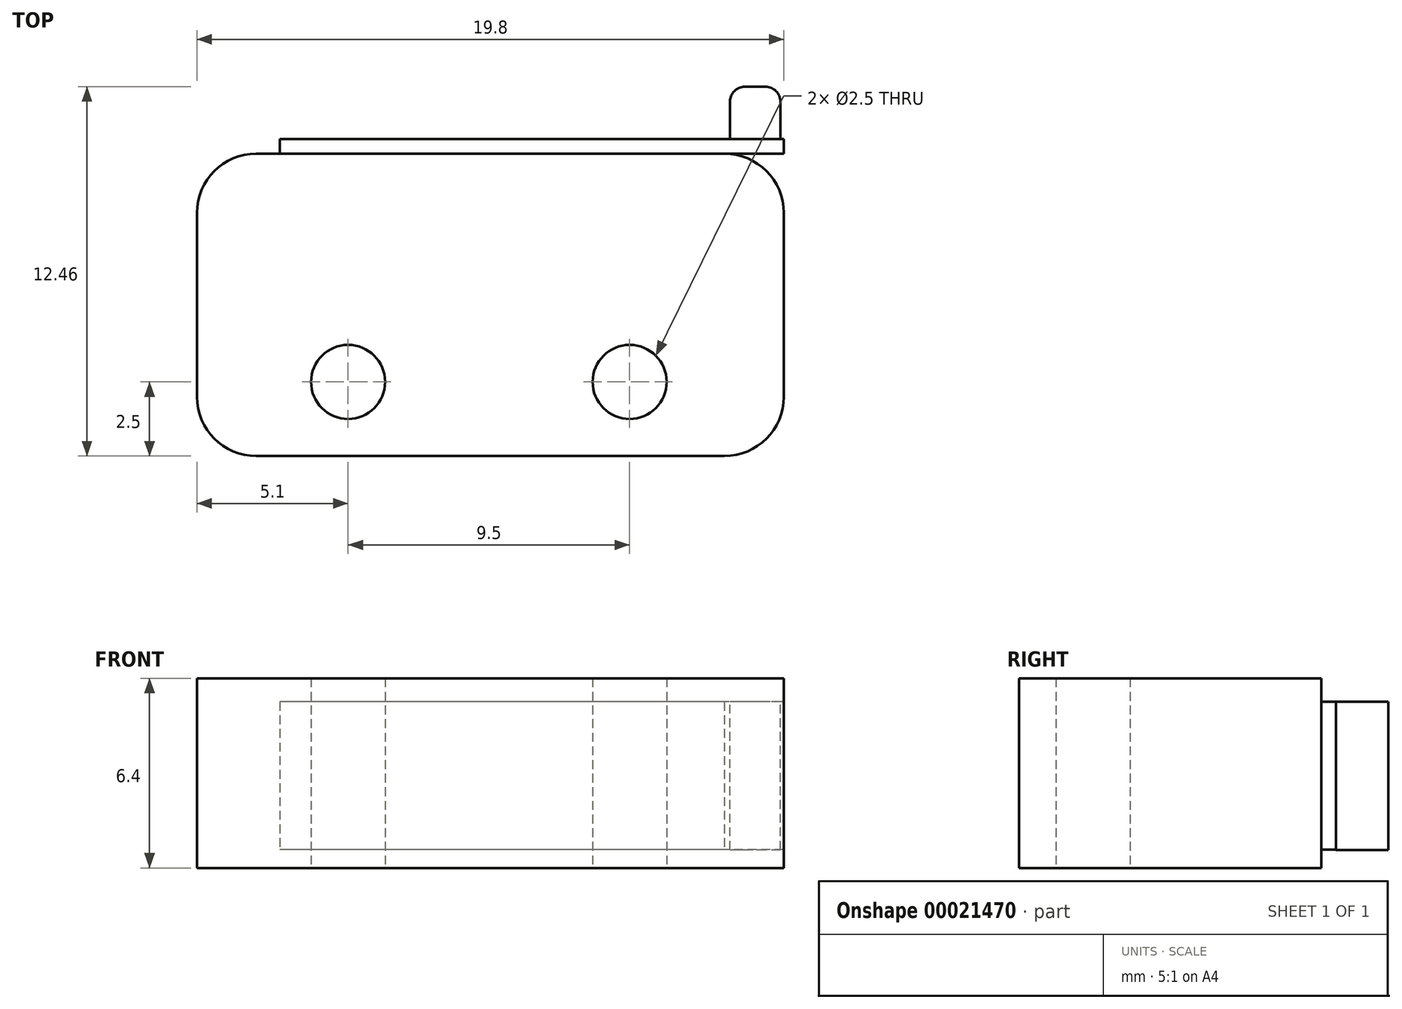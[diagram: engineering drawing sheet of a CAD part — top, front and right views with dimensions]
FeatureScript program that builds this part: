
annotation { "Feature Type Name" : "Feature", "Feature Type Description" : "" }
export const myFeature = defineFeature(function(context is Context, id is Id, definition is map)
    precondition{}
    {
        {
            var Q0;
            Q0=qCreatedBy(makeId("Top.planeOp"),FACE);
            var sketch = newSketch(context, id + "F0", { "sketchPlane" : qUnion([Q0])});
            skLineSegment(sketch, "E0.rect.bottom", {"start": v(9.9, -5.1) * mm, "end": v(-9.9, -5.1) * mm});
            skLineSegment(sketch, "E0.rect.top", {"start": v(9.9, 5.1) * mm, "end": v(-9.9, 5.1) * mm});
            skLineSegment(sketch, "E0.rect.left", {"start": v(9.9, -5.1) * mm, "end": v(9.9, 5.1) * mm});
            skLineSegment(sketch, "E0.rect.right", {"start": v(-9.9, -5.1) * mm, "end": v(-9.9, 5.1) * mm});
            skPoint(sketch, "E0.rect.middle", {"position": v(0, 0) * mm});
            skLineSegment(sketch, "E1", {"start": v(-11.22, -2.6) * mm, "end": v(12.45, -2.6) * mm, "construction": true});
            skCircle(sketch, "E2", {"center": v(-4.8, -2.6) * mm, "radius": 1.25 * mm});
            skCircle(sketch, "E3", {"center": v(4.7, -2.6) * mm, "radius": 1.25 * mm});
            skSolve(sketch);
        }
        {
            var Q0;
            Q0=makeQuery(id+"F0.imprint","IMPRINT",FACE,{"disambiguationData":[TD([[makeQuery(id+"F0.imprint","IMPRINT",EDGE,{"derivedFrom":sQuery(id+"F0.wireOp",EDGE,"E0.rect.bottom")}),-1.0]])]});
            extrude(context, id + "F1", {"entities" : qUnion([Q0]), "depth" : 6.4 * mm});
        }
        {
            var Q0;
            Q0=makeQuery(id+"F1.opExtrude","SWEPT_EDGE",EDGE,{"disambiguationData":[OSD([sQuery(id+"F0.wireOp",EDGE,"E0.rect.top"),sQuery(id+"F0.wireOp",EDGE,"E0.rect.left")])]});
            var Q1;
            Q1=makeQuery(id+"F1.opExtrude","SWEPT_EDGE",EDGE,{"disambiguationData":[OSD([sQuery(id+"F0.wireOp",EDGE,"E0.rect.top"),sQuery(id+"F0.wireOp",EDGE,"E0.rect.right")])]});
            var Q2;
            Q2=makeQuery(id+"F1.opExtrude","SWEPT_EDGE",EDGE,{"disambiguationData":[OSD([sQuery(id+"F0.wireOp",EDGE,"E0.rect.bottom"),sQuery(id+"F0.wireOp",EDGE,"E0.rect.left")])]});
            var Q3;
            Q3=makeQuery(id+"F1.opExtrude","SWEPT_EDGE",EDGE,{"disambiguationData":[OSD([sQuery(id+"F0.wireOp",EDGE,"E0.rect.bottom"),sQuery(id+"F0.wireOp",EDGE,"E0.rect.right")])]});
            fillet(context, id + "F2", {"entities" : qUnion([Q0, Q1, Q2, Q3]), "radius" : 2 * mm, "tangentPropagation" : true, "allowEdgeOverflow" : false});
        }
        {
            var Q0;
            Q0=makeQuery(id+"F1.opExtrude","SWEPT_FACE",FACE,{"disambiguationData":[OSD([sQuery(id+"F0.wireOp",EDGE,"E0.rect.top")])]});
            var sketch = newSketch(context, id + "F3", { "sketchPlane" : qUnion([Q0])});
            skLineSegment(sketch, "E4.rect.bottom", {"start": v(-9.9, 5.6) * mm, "end": v(7.1, 5.6) * mm});
            skLineSegment(sketch, "E4.rect.top", {"start": v(-9.9, 0.62) * mm, "end": v(7.1, 0.62) * mm});
            skLineSegment(sketch, "E4.rect.left", {"start": v(-9.9, 5.6) * mm, "end": v(-9.9, 0.62) * mm});
            skLineSegment(sketch, "E4.rect.right", {"start": v(7.1, 5.6) * mm, "end": v(7.1, 0.62) * mm});
            skPoint(sketch, "E4.rect.middle", {"position": v(-1.4, 3.11) * mm});
            skSolve(sketch);
        }
        {
            var Q0;
            {var subQ7=sQuery(id+"F3.wireOp",EDGE,"E4.rect.left");var subQ8=sQuery(id+"F3.wireOp",EDGE,"E4.rect.right");Q0=qUnion([makeQuery(id+"F3.imprint","IMPRINT",FACE,{"disambiguationData":[TD([[makeQuery(id+"F3.imprint","IMPRINT",EDGE,{"derivedFrom":subQ7}),1.0]])]}),makeQuery(id+"F3.imprint","IMPRINT",FACE,{"disambiguationData":[TD([[makeQuery(id+"F3.imprint","IMPRINT",EDGE,{"derivedFrom":subQ8}),-1.0]])]})]);}
            extrude(context, id + "F4", {"entities" : qUnion([Q0]), "operationType" : NewBodyOperationType.ADD, "depth" : .5 * mm});
        }
        {
            var Q0;
            Q0=makeQuery(id+"F4.opExtrude","SWEPT_FACE",FACE,{"disambiguationData":[OSD([sQuery(id+"F3.wireOp",EDGE,"E4.rect.bottom")])]});
            var sketch = newSketch(context, id + "F5", { "sketchPlane" : qUnion([Q0])});
            skLineSegment(sketch, "E5.rect.bottom", {"start": v(9.78, 5.6) * mm, "end": v(8.09, 5.6) * mm});
            skLineSegment(sketch, "E5.rect.top", {"start": v(9.28, 7.36) * mm, "end": v(8.59, 7.36) * mm});
            skLineSegment(sketch, "E5.rect.left", {"start": v(9.78, 5.6) * mm, "end": v(9.78, 6.86) * mm});
            skLineSegment(sketch, "E5.rect.right", {"start": v(8.09, 5.6) * mm, "end": v(8.09, 6.86) * mm});
            skPoint(sketch, "E5.rect.middle", {"position": v(8.94, 6.48) * mm});
            skPoint(sketch, "E6.visualSharp", {"position": v(8.09, 7.36) * mm});
            skArc(sketch, "E6.filletArc", {"start": v(8.59, 7.36) * mm, "mid": v(8.23, 7.21) * mm, "end": v(8.09, 6.86) * mm});
            skPoint(sketch, "E7.visualSharp", {"position": v(9.78, 7.36) * mm});
            skArc(sketch, "E7.filletArc", {"start": v(9.78, 6.86) * mm, "mid": v(9.64, 7.21) * mm, "end": v(9.28, 7.36) * mm});
            skSolve(sketch);
        }
        {
            var Q0;
            Q0=qSketchRegion(id+"F5",true);
            extrude(context, id + "F6", {"entities" : qUnion([Q0]), "oppositeDirection" : true, "depth" : 5 * mm});
        }
    });
